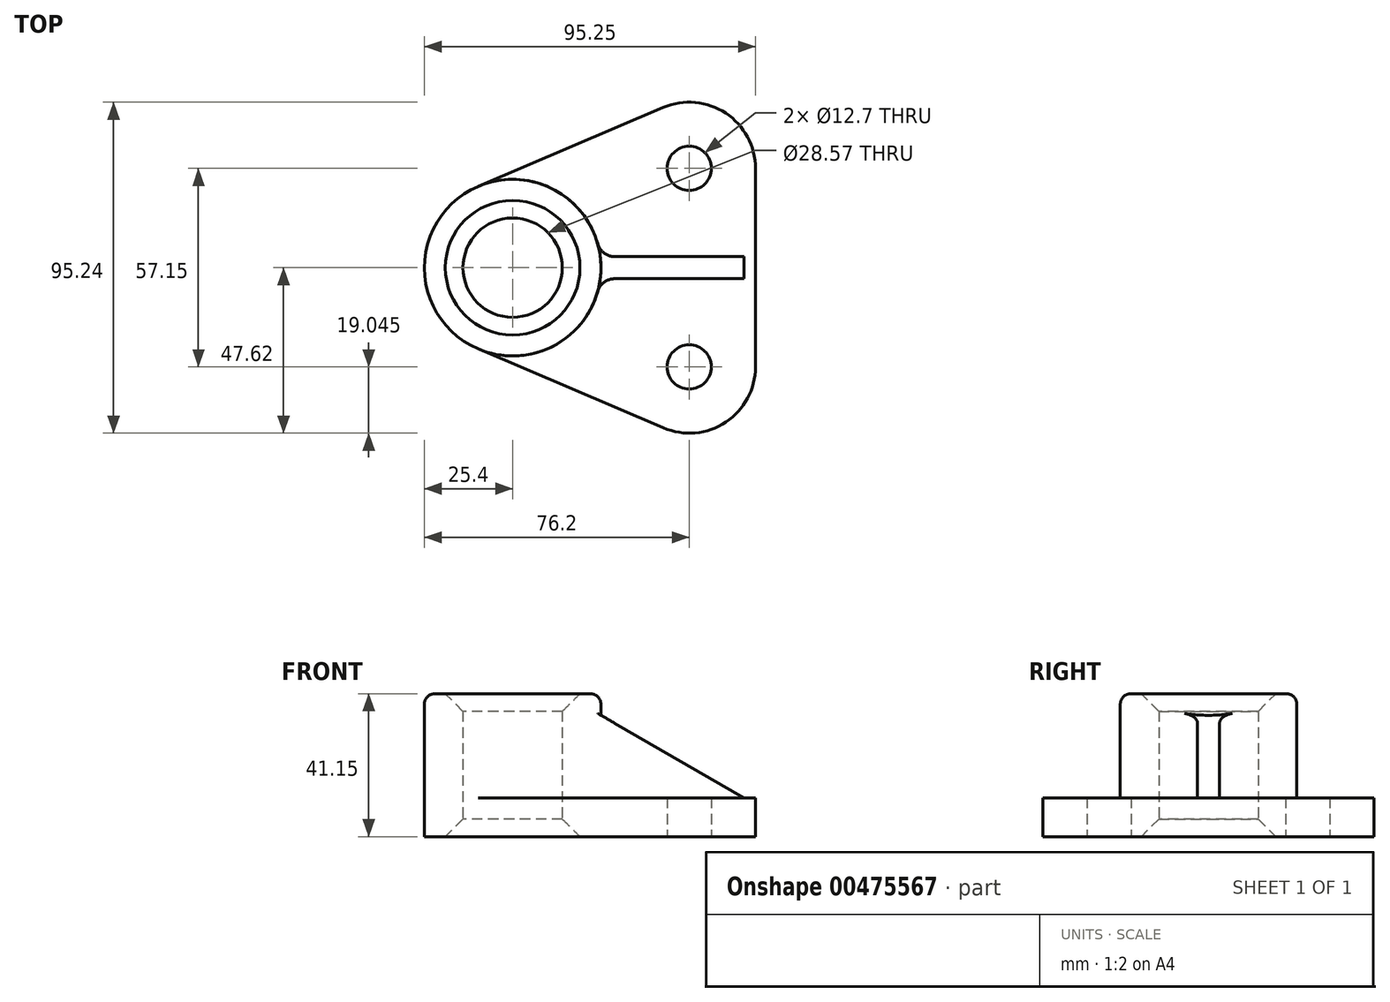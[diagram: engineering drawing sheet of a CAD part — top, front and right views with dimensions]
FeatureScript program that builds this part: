
annotation { "Feature Type Name" : "Feature", "Feature Type Description" : "" }
export const myFeature = defineFeature(function(context is Context, id is Id, definition is map)
    precondition{}
    {
        {
            var Q0;
            Q0=qCreatedBy(makeId("Top.planeOp"),FACE);
            var sketch = newSketch(context, id + "F0", { "sketchPlane" : qUnion([Q0])});
            skCircle(sketch, "E0", {"center": v(0, 0) * mm, "radius": 25.4 * mm});
            skCircle(sketch, "E1", {"center": v(0, 0) * mm, "radius": 14.29 * mm});
            skCircle(sketch, "E2", {"center": v(50.8, 28.58) * mm, "radius": 6.35 * mm});
            skCircle(sketch, "E3", {"center": v(50.8, -28.58) * mm, "radius": 6.35 * mm});
            skCircle(sketch, "E4", {"center": v(50.8, 28.58) * mm, "radius": 19.05 * mm});
            skCircle(sketch, "E5", {"center": v(50.8, -28.58) * mm, "radius": 19.05 * mm});
            skLineSegment(sketch, "E6", {"start": v(-9.97, 23.36) * mm, "end": v(43.33, 46.1) * mm});
            skLineSegment(sketch, "E7", {"start": v(-9.97, -23.36) * mm, "end": v(43.33, -46.1) * mm});
            skLineSegment(sketch, "E8", {"start": v(69.85, 28.58) * mm, "end": v(69.85, -28.57) * mm});
            skSolve(sketch);
        }
        {
            var Q0;
            Q0=makeQuery(id+"F0.imprint","IMPRINT",FACE,{"disambiguationData":[TD([[makeQuery(id+"F0.imprint","IMPRINT",EDGE,{"derivedFrom":sQuery(id+"F0.wireOp",EDGE,"E1")}),-1.0]])]});
            extrude(context, id + "F1", {"entities" : qUnion([Q0]), "depth" : 41.15 * mm});
        }
        {
            var Q0;
            {var subQ0=sQuery(id+"F0.wireOp",EDGE,"E6");Q0=makeQuery(id+"F0.imprint","IMPRINT",FACE,{"disambiguationData":[TD([[makeQuery(id+"F0.imprint","IMPRINT",EDGE,{"derivedFrom":subQ0}),-1.0]])]});}
            var Q1;
            Q1=makeQuery(id+"F0.imprint","IMPRINT",FACE,{"disambiguationData":[TD([[makeQuery(id+"F0.imprint","IMPRINT",EDGE,{"derivedFrom":sQuery(id+"F0.wireOp",EDGE,"E2")}),-1.0]])]});
            var Q2;
            Q2=makeQuery(id+"F0.imprint","IMPRINT",FACE,{"disambiguationData":[TD([[makeQuery(id+"F0.imprint","IMPRINT",EDGE,{"derivedFrom":sQuery(id+"F0.wireOp",EDGE,"E3")}),-1.0]])]});
            extrude(context, id + "F2", {"entities" : qUnion([Q0, Q1, Q2]), "operationType" : NewBodyOperationType.ADD, "depth" : 11.18 * mm});
        }
        {
            var Q0;
            Q0=qCreatedBy(makeId("Front.planeOp"),FACE);
            var sketch = newSketch(context, id + "F3", { "sketchPlane" : qUnion([Q0])});
            skLineSegment(sketch, "E9", {"start": v(19.05, 38.6) * mm, "end": v(66.55, 11.18) * mm});
            skLineSegment(sketch, "E10", {"start": v(66.55, 11.18) * mm, "end": v(19.05, 11.18) * mm});
            skLineSegment(sketch, "E11", {"start": v(19.05, 11.18) * mm, "end": v(19.05, 38.6) * mm});
            skSolve(sketch);
        }
        {
            var Q0;
            Q0=makeQuery(id+"F3.imprint","IMPRINT",FACE,{"disambiguationData":[TD([[makeQuery(id+"F3.imprint","IMPRINT",EDGE,{"derivedFrom":sQuery(id+"F3.wireOp",EDGE,"E9")}),-1.0]])]});
            extrude(context, id + "F4", {"entities" : qUnion([Q0]), "operationType" : NewBodyOperationType.ADD, "depth" : 3.17 * mm, "hasSecondDirection" : true, "secondDirectionOppositeDirection" : true, "secondDirectionDepth" : 3.17 * mm});
        }
        {
            var Q0;
            Q0=makeQuery(id+"F1.opExtrude","CAP_EDGE",EDGE,{"disambiguationData":[OSD([sQuery(id+"F0.wireOp",EDGE,"E0")])],"isStart":false});
            fillet(context, id + "F5", {"entities" : qUnion([Q0]), "radius" : 3.05 * mm, "tangentPropagation" : true, "allowEdgeOverflow" : false});
        }
        {
            var Q0;
            {var subQ0=sQuery(id+"F0.wireOp",EDGE,"E0");var subQ1=sQuery(id+"F0.wireOp",EDGE,"E7");Q0=makeQuery(id+"F4.boolean.opBoolean","SPLIT",EDGE,{"disambiguationData":[TD([makeQuery(id+"F2.opExtrude","SWEPT_FACE",FACE,{"disambiguationData":[OSD([subQ1])]})])],"derivedFrom":makeQuery(id+"F2.opExtrude","CAP_EDGE",EDGE,{"disambiguationData":[OSD([subQ0])],"isStart":false})});}
            var Q1;
            Q1=makeQuery(id+"F4.opExtrude","CAP_EDGE",EDGE,{"disambiguationData":[OSD([sQuery(id+"F3.wireOp",EDGE,"E10")])],"isStart":false});
            var Q2;
            Q2=makeQuery(id+"F4.opExtrude","CAP_EDGE",EDGE,{"disambiguationData":[OSD([sQuery(id+"F3.wireOp",EDGE,"E10")])],"isStart":true});
            var Q3;
            {var subQ0=sQuery(id+"F0.wireOp",EDGE,"E0");var subQ1=sQuery(id+"F0.wireOp",EDGE,"E6");Q3=makeQuery(id+"F4.boolean.opBoolean","SPLIT",EDGE,{"disambiguationData":[TD([makeQuery(id+"F2.opExtrude","SWEPT_FACE",FACE,{"disambiguationData":[OSD([subQ1])]})])],"derivedFrom":makeQuery(id+"F2.opExtrude","CAP_EDGE",EDGE,{"disambiguationData":[OSD([subQ0])],"isStart":false})});}
            var Q4;
            Q4=makeQuery(id+"F4.boolean.opBoolean","INTERSECT",EDGE,{"derivedFrom":[makeQuery(id+"F1.opExtrude","SWEPT_FACE",FACE,{"disambiguationData":[OSD([sQuery(id+"F0.wireOp",EDGE,"E0")])]}),makeQuery(id+"F4.opExtrude","CAP_FACE",FACE,{"disambiguationData":[OSD([sQuery(id+"F3.wireOp",EDGE,"E9"),sQuery(id+"F3.wireOp",EDGE,"E10"),sQuery(id+"F3.wireOp",EDGE,"E11")])],"isStart":true})]});
            var Q5;
            Q5=makeQuery(id+"F4.boolean.opBoolean","INTERSECT",EDGE,{"derivedFrom":[makeQuery(id+"F1.opExtrude","SWEPT_FACE",FACE,{"disambiguationData":[OSD([sQuery(id+"F0.wireOp",EDGE,"E0")])]}),makeQuery(id+"F4.opExtrude","CAP_FACE",FACE,{"disambiguationData":[OSD([sQuery(id+"F3.wireOp",EDGE,"E9"),sQuery(id+"F3.wireOp",EDGE,"E10"),sQuery(id+"F3.wireOp",EDGE,"E11")])],"isStart":false})]});
            fillet(context, id + "F6", {"entities" : qUnion([Q0, Q1, Q2, Q3, Q4, Q5]), "radius" : 5.08 * mm, "tangentPropagation" : true, "allowEdgeOverflow" : false});
        }
        {
            var Q0;
            Q0=makeQuery(id+"F1.opExtrude","CAP_EDGE",EDGE,{"disambiguationData":[OSD([sQuery(id+"F0.wireOp",EDGE,"E1")])],"isStart":false});
            var Q1;
            Q1=makeQuery(id+"F1.opExtrude","CAP_EDGE",EDGE,{"disambiguationData":[OSD([sQuery(id+"F0.wireOp",EDGE,"E1")])],"isStart":true});
            chamfer(context, id + "F7", {"entities" : qUnion([Q0, Q1]), "chamferType" : ChamferType.OFFSET_ANGLE, "width" : 5.08 * mm, "oppositeDirection" : false, "angle" : 45 * degree, "tangentPropagation" : true});
        }
    });
